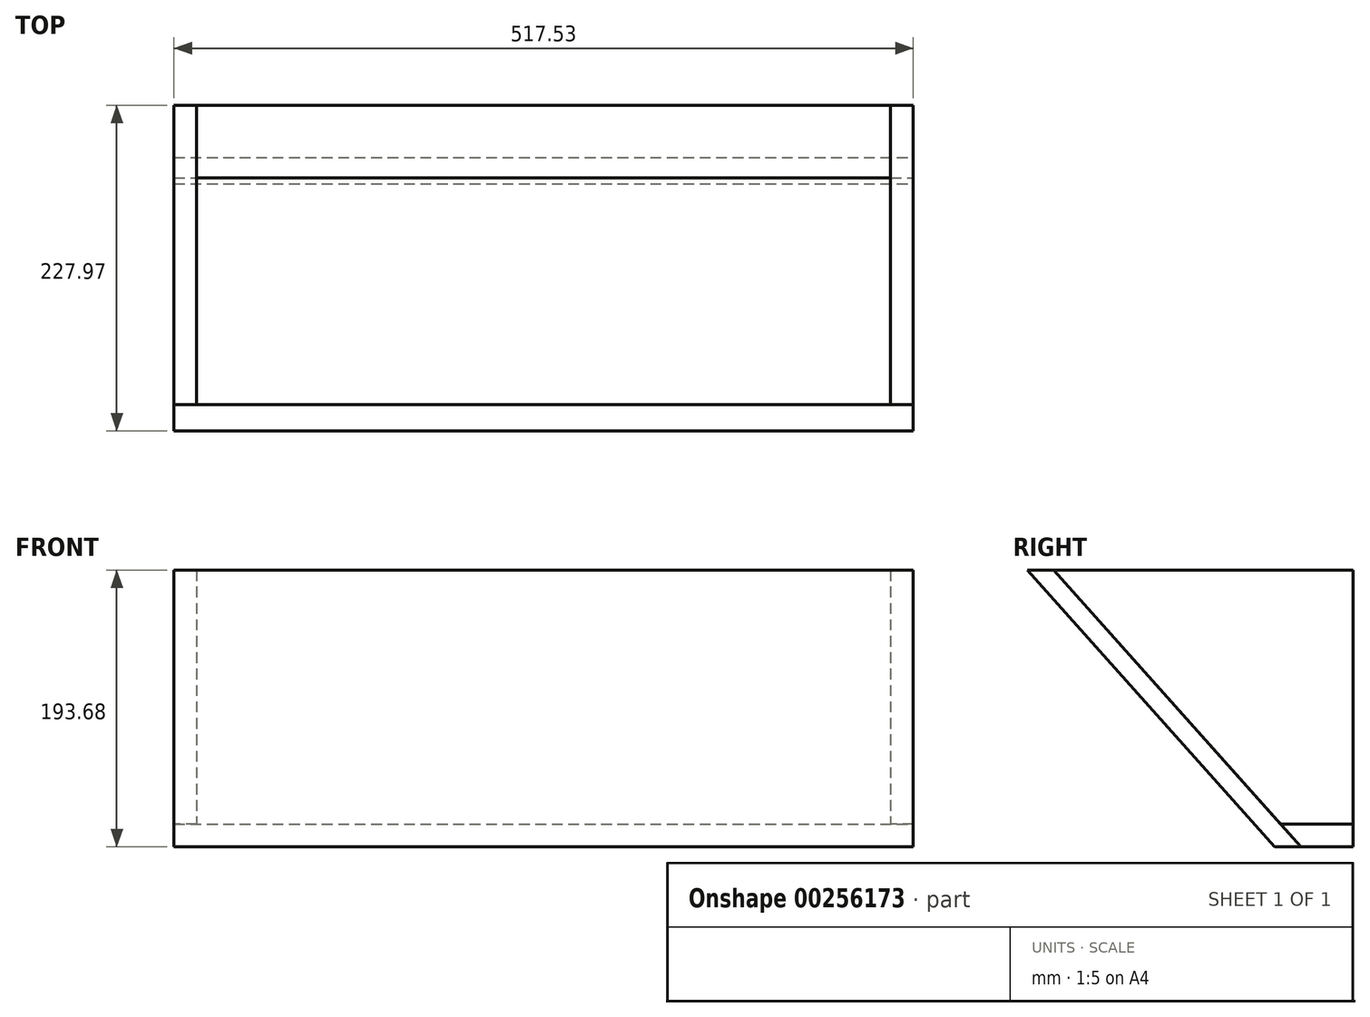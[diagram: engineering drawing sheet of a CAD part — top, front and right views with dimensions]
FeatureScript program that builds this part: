
annotation { "Feature Type Name" : "Feature", "Feature Type Description" : "" }
export const myFeature = defineFeature(function(context is Context, id is Id, definition is map)
    precondition{}
    {
        {
            var Q0;
            Q0=qCreatedBy(makeId("Right.planeOp"),FACE);
            var sketch = newSketch(context, id + "F0", { "sketchPlane" : qUnion([Q0])});
            skLineSegment(sketch, "E0", {"start": v(0, 0) * mm, "end": v(-50.8, 0) * mm});
            skLineSegment(sketch, "E1", {"start": v(-50.8, 0) * mm, "end": v(-209.55, 177.8) * mm});
            skLineSegment(sketch, "E2", {"start": v(-209.55, 177.8) * mm, "end": v(0, 177.8) * mm});
            skLineSegment(sketch, "E3", {"start": v(0, 177.8) * mm, "end": v(0, 0) * mm});
            skSolve(sketch);
        }
        {
            var Q0;
            Q0=qSketchRegion(id+"F0",true);
            extrude(context, id + "F1", {"entities" : qUnion([Q0]), "depth" : 15.88 * mm});
        }
        {
            var Q0;
            Q0=makeQuery(id+"F1.opExtrude","CAP_FACE",FACE,{"disambiguationData":[OSD([sQuery(id+"F0.wireOp",EDGE,"E0"),sQuery(id+"F0.wireOp",EDGE,"E1"),sQuery(id+"F0.wireOp",EDGE,"E2"),sQuery(id+"F0.wireOp",EDGE,"E3")])],"isStart":false});
            var sketch = newSketch(context, id + "F2", { "sketchPlane" : qUnion([Q0])});
            skSolve(sketch);
        }
        {
            var Q0;
            Q0=makeQuery(id+"F2.imprint","IMPRINT",FACE,{"disambiguationData":[TD([[makeQuery(id+"F2.imprint","IMPRINT",EDGE,{"derivedFrom":makeQuery(id+"F1.opExtrude","CAP_EDGE",EDGE,{"disambiguationData":[OSD([sQuery(id+"F0.wireOp",EDGE,"E0")])],"isStart":false})}),-1.0]])]});
            var sketch = newSketch(context, id + "F3", { "sketchPlane" : qUnion([Q0])});
            skLineSegment(sketch, "E4", {"start": v(0, 0) * mm, "end": v(0, -15.88) * mm});
            skLineSegment(sketch, "E5", {"start": v(0, -15.88) * mm, "end": v(-36.63, -15.88) * mm});
            skLineSegment(sketch, "E6", {"start": v(-36.63, -15.88) * mm, "end": v(-50.8, 0) * mm});
            skLineSegment(sketch, "E7", {"start": v(-50.8, 0) * mm, "end": v(0, 0) * mm});
            skSolve(sketch);
        }
        {
            var Q0;
            Q0=qSketchRegion(id+"F3",true);
            extrude(context, id + "F4", {"entities" : qUnion([Q0]), "oppositeDirection" : true, "depth" : 517.52 * mm});
        }
        {
            var Q0;
            Q0=makeQuery(id+"F2.imprint","IMPRINT",FACE,{"disambiguationData":[TD([[makeQuery(id+"F2.imprint","IMPRINT",EDGE,{"derivedFrom":makeQuery(id+"F1.opExtrude","CAP_EDGE",EDGE,{"disambiguationData":[OSD([sQuery(id+"F0.wireOp",EDGE,"E0")])],"isStart":false})}),-1.0]])]});
            var sketch = newSketch(context, id + "F5", { "sketchPlane" : qUnion([Q0])});
            skLineSegment(sketch, "E8", {"start": v(-209.55, 177.8) * mm, "end": v(-227.97, 177.8) * mm});
            skLineSegment(sketch, "E9", {"start": v(-227.97, 177.8) * mm, "end": v(-55.05, -15.88) * mm});
            skLineSegment(sketch, "E10", {"start": v(-55.05, -15.88) * mm, "end": v(-36.63, -15.88) * mm});
            skLineSegment(sketch, "E11", {"start": v(-36.63, -15.88) * mm, "end": v(-209.55, 177.8) * mm});
            skSolve(sketch);
        }
        {
            var Q0;
            Q0=qSketchRegion(id+"F5",true);
            extrude(context, id + "F6", {"entities" : qUnion([Q0]), "oppositeDirection" : true, "depth" : 517.52 * mm});
        }
        {
            var Q0;
            Q0=makeQuery(id+"F1.opExtrude","SWEPT_BODY",BODY,{"disambiguationData":[OSD([sQuery(id+"F0.wireOp",EDGE,"E0"),sQuery(id+"F0.wireOp",EDGE,"E1"),sQuery(id+"F0.wireOp",EDGE,"E2"),sQuery(id+"F0.wireOp",EDGE,"E3")])]});
            transform(context, id + "F7", {"entities" : qUnion([Q0]), "transformType" : TransformType.TRANSLATION_3D, "dx" : -501.65 * mm, "dy" : 0 * mm, "dz" : 0 * mm, "makeCopy" : true});
        }
    });
